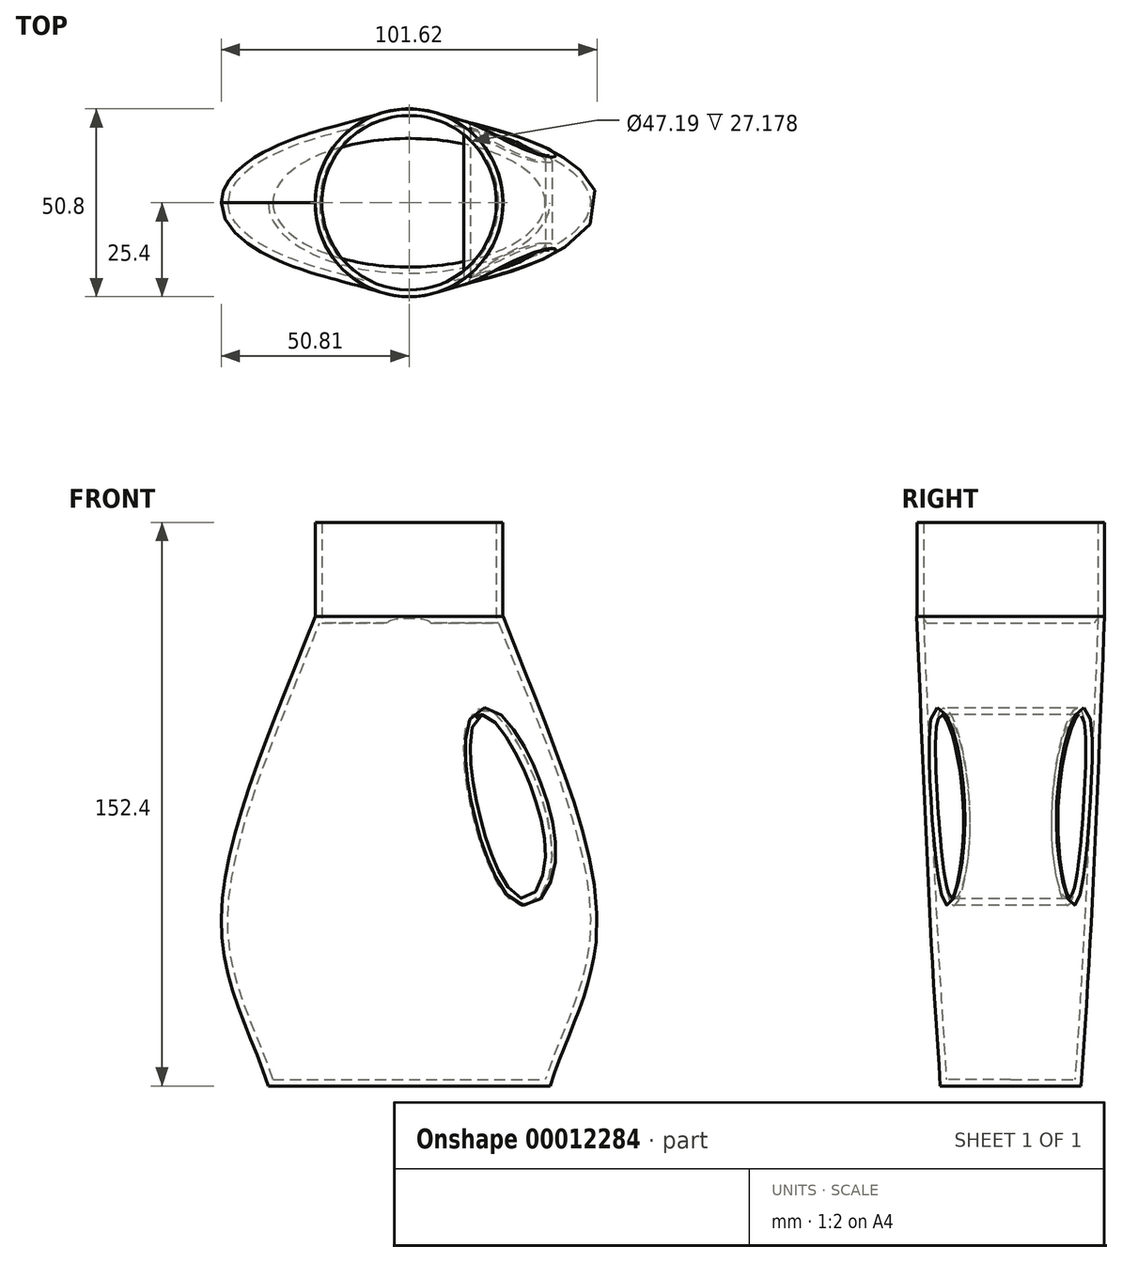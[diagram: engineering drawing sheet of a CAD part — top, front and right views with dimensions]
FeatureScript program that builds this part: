
annotation { "Feature Type Name" : "Feature", "Feature Type Description" : "" }
export const myFeature = defineFeature(function(context is Context, id is Id, definition is map)
    precondition{}
    {
        {
            var Q0;
            Q0=qCreatedBy(makeId("Top.planeOp"),FACE);
            var sketch = newSketch(context, id + "F0", { "sketchPlane" : qUnion([Q0])});
            skEllipse(sketch, "E0", {"center": v(0, 0) * mm, "majorRadius": 38.1 * mm, "minorRadius": 19.05 * mm, "majorAxis": v(1, 0)});
            skSolve(sketch);
        }
        {
            var Q0;
            Q0=qCreatedBy(makeId("Front.planeOp"),FACE);
            var sketch = newSketch(context, id + "F1", { "sketchPlane" : qUnion([Q0])});
            skLineSegment(sketch, "E1", {"start": v(0, 0) * mm, "end": v(0, 212.82) * mm, "construction": true});
            skFitSpline(sketch, "E2", {"points": [v(38.1, 0) * mm, v(50.8, 43.18) * mm, v(25.4, 127) * mm], "startDerivative": vector(30.53, 97.94) * mm, "endDerivative": vector(-58.7, 153.1) * mm});
            skFitSpline(sketch, "E3.0.MirrorCS", {"points": [v(-38.1, 0) * mm, v(-50.8, 43.18) * mm, v(-25.4, 127) * mm], "startDerivative": vector(-30.53, 97.94) * mm, "endDerivative": vector(58.7, 153.1) * mm});
            skSolve(sketch);
        }
        {
            var Q0;
            Q0=qCreatedBy(makeId("Top.planeOp"),FACE);
            cPlane(context, id + "F2", {"entities" : qUnion([Q0]), "cplaneType" : CPlaneType.OFFSET, "offset" : 127 * mm, "width" : 152.4 * mm, "height" : 152.4 * mm});
        }
        {
            var Q0;
            Q0=qCreatedBy(id+"F2.planeOp",FACE);
            var sketch = newSketch(context, id + "F3", { "sketchPlane" : qUnion([Q0])});
            skCircle(sketch, "E4", {"center": v(0, 0) * mm, "radius": 25.4 * mm});
            skSolve(sketch);
        }
        {
            var Q0;
            Q0=makeQuery(id+"F0.imprint","IMPRINT",FACE,{"disambiguationData":[TD([[makeQuery(id+"F0.imprint","IMPRINT",EDGE,{"derivedFrom":sQuery(id+"F0.wireOp",EDGE,"E0")}),1.0]])]});
            var Q1;
            Q1=makeQuery(id+"F3.imprint","IMPRINT",FACE,{"disambiguationData":[TD([[makeQuery(id+"F3.imprint","IMPRINT",EDGE,{"derivedFrom":sQuery(id+"F3.wireOp",EDGE,"E4")}),1.0]])]});
            var Q2;
            Q2=sQuery(id+"F1.wireOp",EDGE,"E3.0.MirrorCS");
            var Q3;
            Q3=sQuery(id+"F1.wireOp",EDGE,"E2");
            loft(context, id + "F4", {"addGuides" : true, "sheetProfilesArray" : [{ "sheetProfileEntities" : qUnion([Q0]) }, { "sheetProfileEntities" : qUnion([Q1]) }], "guidesArray" : [{ "guideEntities" : qUnion([Q2]), "guideDerivativeType" : LoftGuideDerivativeType.DEFAULT, "guideDerivativeMagnitude" : 1 }, { "guideEntities" : qUnion([Q3]), "guideDerivativeType" : LoftGuideDerivativeType.DEFAULT, "guideDerivativeMagnitude" : 1 }]});
        }
        {
            var Q0;
            Q0=qCreatedBy(id+"F2.planeOp",FACE);
            var sketch = newSketch(context, id + "F5", { "sketchPlane" : qUnion([Q0])});
            skCircle(sketch, "E5", {"center": v(0, 0) * mm, "radius": 25.37 * mm});
            skSolve(sketch);
        }
        {
            var Q0;
            Q0=makeQuery(id+"F5.imprint","IMPRINT",FACE,{"disambiguationData":[TD([[makeQuery(id+"F5.imprint","IMPRINT",EDGE,{"derivedFrom":sQuery(id+"F5.wireOp",EDGE,"E5")}),1.0]])]});
            extrude(context, id + "F6", {"entities" : qUnion([Q0]), "operationType" : NewBodyOperationType.ADD, "depth" : 25.4 * mm});
        }
        {
            var Q0;
            Q0=qCreatedBy(makeId("Front.planeOp"),FACE);
            var sketch = newSketch(context, id + "F7", { "sketchPlane" : qUnion([Q0])});
            skFitSpline(sketch, "E6", {"points": [v(20.44, 100.27) * mm, v(16.61, 88.07) * mm, v(30.01, 50.83) * mm, v(36.85, 63.74) * mm, v(20.44, 100.27) * mm]});
            skSolve(sketch);
        }
        {
            var Q0;
            Q0 = qSketchRegion(id + "F7", true);
            extrude(context, id + "F8", {"entities" : qUnion([Q0]), "operationType" : NewBodyOperationType.REMOVE, "endBound" : BoundingType.SYMMETRIC, "oppositeDirection" : true, "depth" : 44.6 * mm});
        }
        {
            var Q0;
            Q0=makeQuery(id+"F8.boolean.opBoolean","INTERSECT",EDGE,{"disambiguationData":[OD(0.0)],"derivedFrom":[makeQuery(id+"F4.opLoft","SWEPT_FACE",FACE,{"disambiguationData":[OSD([sQuery(id+"F0.wireOp",EDGE,"E0"),sQuery(id+"F1.wireOp",EDGE,"E2"),sQuery(id+"F1.wireOp",EDGE,"E3.0.MirrorCS"),sQuery(id+"F3.wireOp",EDGE,"E4")])]}),makeQuery(id+"F8.opExtrude","SWEPT_FACE",FACE,{"disambiguationData":[OSD([sQuery(id+"F7.wireOp",EDGE,"E6")])]})]});
            var Q1;
            Q1=makeQuery(id+"F8.boolean.opBoolean","INTERSECT",EDGE,{"disambiguationData":[OD(1.0)],"derivedFrom":[makeQuery(id+"F4.opLoft","SWEPT_FACE",FACE,{"disambiguationData":[OSD([sQuery(id+"F0.wireOp",EDGE,"E0"),sQuery(id+"F1.wireOp",EDGE,"E2"),sQuery(id+"F1.wireOp",EDGE,"E3.0.MirrorCS"),sQuery(id+"F3.wireOp",EDGE,"E4")])]}),makeQuery(id+"F8.opExtrude","SWEPT_FACE",FACE,{"disambiguationData":[OSD([sQuery(id+"F7.wireOp",EDGE,"E6")])]})]});
            fillet(context, id + "F9", {"entities" : qUnion([Q0, Q1]), "radius" : 1.78 * mm, "tangentPropagation" : true, "allowEdgeOverflow" : false});
        }
        {
            var Q0;
            Q0=makeQuery(id+"F6.opExtrude","CAP_FACE",FACE,{"disambiguationData":[OSD([sQuery(id+"F5.wireOp",EDGE,"E5")])],"isStart":false});
            shell(context, id + "F10", {"entities" : qUnion([Q0]), "thickness" : 1.78 * mm});
        }
    });
